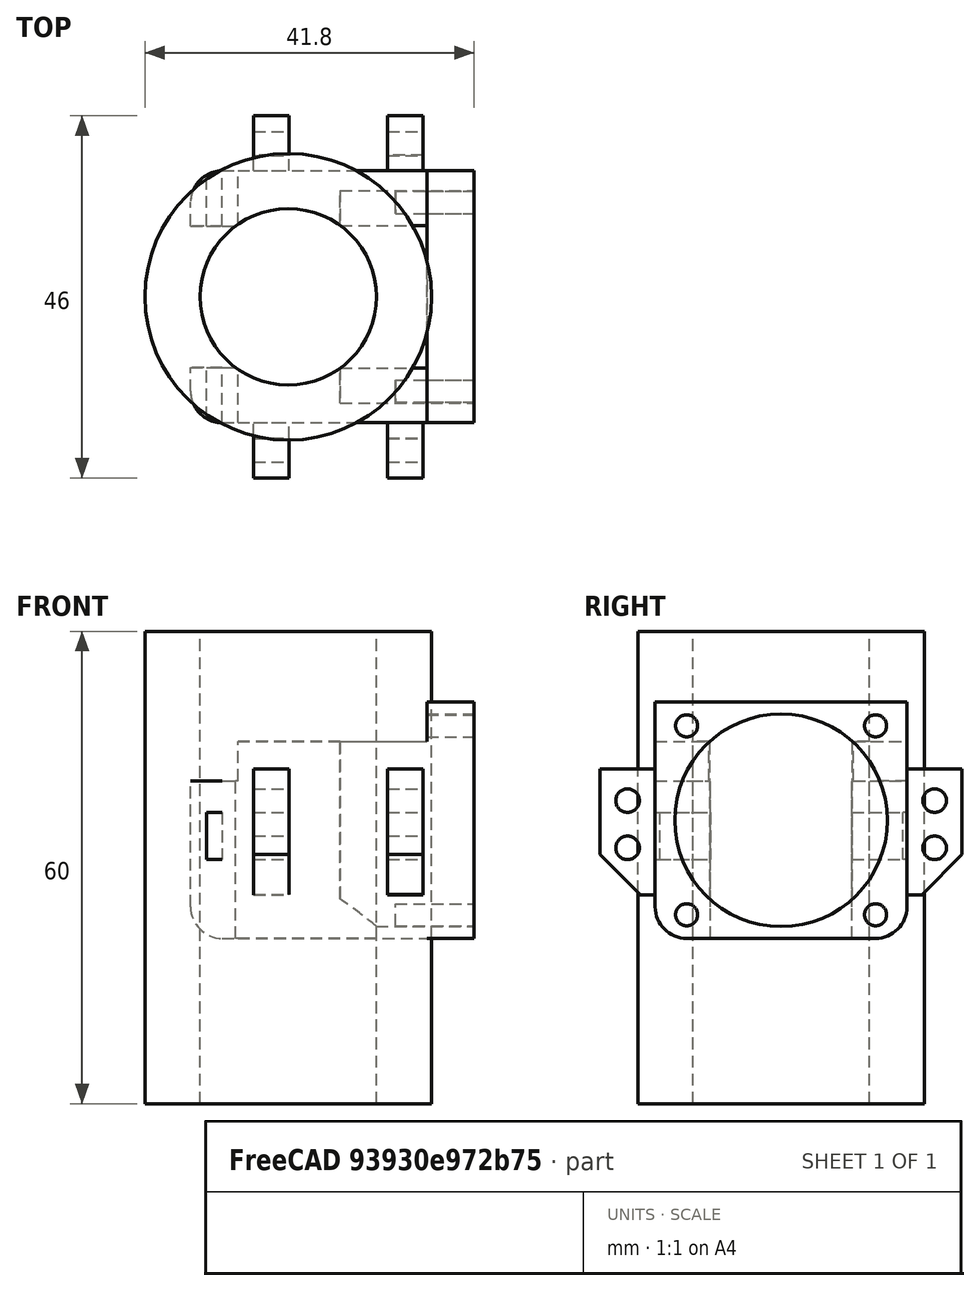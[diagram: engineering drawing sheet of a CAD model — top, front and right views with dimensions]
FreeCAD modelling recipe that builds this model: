
FCSTD DOCUMENT  (FreeCAD 0.15R4671 (Git))
Label: e3dv6
License: All rights reserved
LicenseURL: http://en.wikipedia.org/wiki/All_rights_reserved
objects: Part::Box×13, Part::Cylinder×12, Part::MultiFuse×6, Part::Fillet×4, Part::Cut×3, Mesh::Feature×2, Part::Feature×2
note: 40 computed .brp shape members not serialized (recipe doc carries the construction recipe); baked Part::Feature solids carry a one-line shape summary decoded from their .brp

FEATURE [Part::Box] Box  label="CubeMain"
  Height = 25
  Length = 24
  Width = 32
FEATURE [Part::Box] Box001  label="CubeFrontMask"
  Height = 30
  Length = 6
  Placement = pos=(24,0,0) rot=(0,0,1;0rad)
  Width = 32
FEATURE [Part::Cylinder] Cylinder  label="CylinderHeatSink"
  Angle = 360
  Height = 25
  Placement = pos=(6.4,16,0) rot=(0,0,1;0rad)
  Radius = 11.2
FEATURE [Part::Cylinder] Cylinder001  label="CylinderFan"
  Angle = 360
  Height = 18
  Placement = pos=(13,16,15) rot=(0,1,0;1.5708rad)
  Radius = 13.5
FEATURE [Part::Cylinder] Cylinder002  label="CylinderBL"
  Angle = 360
  Height = 20
  Placement = pos=(20,4,3) rot=(0,1,0;1.5708rad)
  Radius = 1.4
FEATURE [Part::Cylinder] Cylinder003  label="CylinderTL"
  Angle = 360
  Height = 20
  Placement = pos=(20,4,27) rot=(0,1,0;1.5708rad)
  Radius = 1.4
FEATURE [Part::Cylinder] Cylinder004  label="CylinderTB"
  Angle = 360
  Height = 20
  Placement = pos=(20,28,27) rot=(0,1,0;1.5708rad)
  Radius = 1.4
FEATURE [Part::Cylinder] Cylinder005  label="CylinderRB"
  Angle = 360
  Height = 20
  Placement = pos=(20,28,3) rot=(0,1,0;1.5708rad)
  Radius = 1.4
FEATURE [Part::MultiFuse] Fusion001  label="FusionFanScrews"
  Shapes = -> [Cylinder002,Cylinder003,Cylinder005,Cylinder004]
FEATURE [Part::Box] Box002  label="CubeZipTieL"
  Height = 20
  Length = 6
  Placement = pos=(-6,0,0) rot=(0,0,1;0rad)
  Width = 7
FEATURE [Part::Box] Box003  label="CubZipTieR"
  Height = 20
  Length = 6
  Placement = pos=(-6,25,0) rot=(0,0,1;0rad)
  Width = 7
FEATURE [Part::Box] Box004  label="CubeZipTieHor"
  Height = 6
  Length = 2
  Placement = pos=(-4,0,10) rot=(0,0,1;0rad)
  Width = 32
FEATURE [Part::Cylinder] Cylinder009
  Angle = 360
  Height = 40
  Placement = pos=(0,-3.5,12) rot=(0,1,0;1.5708rad)
  Radius = 1.5
FEATURE [Part::Cylinder] Cylinder010
  Angle = 360
  Height = 40
  Placement = pos=(0,-3.5,6) rot=(0,1,0;1.5708rad)
  Radius = 1.5
FEATURE [Part::Box] Box005  label="Cube005"
  Height = 16
  Length = 4.5
  Placement = pos=(2,-7,0) rot=(0,0,1;0rad)
  Width = 7
FEATURE [Part::Box] Box006  label="Cube006"
  Height = 16
  Length = 4.5
  Placement = pos=(19,-7,0) rot=(0,0,1;0rad)
  Width = 7
FEATURE [Part::Box] Box007  label="Cube007"
  Height = 16
  Length = 4.5
  Placement = pos=(2,32,0) rot=(0,0,1;0rad)
  Width = 7
FEATURE [Part::Box] Box008  label="Cube008"
  Height = 16
  Length = 4.5
  Placement = pos=(19,32,0) rot=(0,0,1;0rad)
  Width = 7
FEATURE [Part::Cylinder] Cylinder011
  Angle = 360
  Height = 40
  Placement = pos=(0,35.5,12) rot=(0,1,0;1.5708rad)
  Radius = 1.5
FEATURE [Part::Cylinder] Cylinder012
  Angle = 360
  Height = 40
  Placement = pos=(0,35.5,6) rot=(0,1,0;1.5708rad)
  Radius = 1.5
FEATURE [Part::MultiFuse] Fusion004  label="FusionWingScrews"
  Placement = pos=(0,0,5.5) rot=(0,0,1;0rad)
  Shapes = -> [Cylinder009,Cylinder010,Cylinder011,Cylinder012]
FEATURE [Part::Box] Box009  label="Cube009"
  Height = 10
  Length = 22
  Placement = pos=(2,-9,-7) rot=(1,0,0;0.785398rad)
  Width = 10
FEATURE [Part::Box] Box010  label="Cube010"
  Height = 10
  Length = 22
  Placement = pos=(2,41,-7) rot=(1,0,0;0.785398rad)
  Width = 10
FEATURE [Part::MultiFuse] Fusion006  label="FusionWings"
  Placement = pos=(0,0,5.5) rot=(0,0,1;0rad)
  Shapes = -> [Box005,Box006,Box007,Box008]
FEATURE [Part::MultiFuse] Fusion005  label="FusionWingCuts"
  Placement = pos=(0,0,5.5) rot=(0,0,1;0rad)
  Shapes = -> [Box009,Box010]
FEATURE [Part::MultiFuse] Fusion  label="FusionCUTS"
  Shapes = -> [Fusion001,Fusion005,Fusion004,Box004,Cylinder,Cylinder001]
FEATURE [Part::MultiFuse] Fusion007  label="FusionMain"
  Shapes = -> [Box,Box002,Fusion006,Box003,Box001]
FEATURE [Part::Fillet] Fillet
  Base = -> Fusion007
  Edges = 1 edges r=4: [Edge86]
FEATURE [Part::Fillet] Fillet001
  Base = -> Fillet
  Edges = 1 edges r=4: [Edge11]
FEATURE [Part::Fillet] Fillet002
  Base = -> Fillet001
  Edges = 1 edges r=4: [Edge66]
FEATURE [Part::Fillet] Fillet003
  Base = -> Fillet002
  Edges = 1 edges r=4: [Edge16]
FEATURE [Part::Cut] Cut  label="CutE3DV6Holder"
  Base = -> Fillet003
  Tool = -> Fusion
FEATURE [Mesh::Feature] E3D_v5_40mm_Duct
FEATURE [Part::Feature] E3D_v5_40mm_Duct001
  Placement = pos=(-37.5,50,14.2) rot=(0,0.965926,-0.258819;3.14159rad)
  shape: large baked B-rep (38 MB .brp); summary skipped
FEATURE [Part::Cylinder] Cylinder014  label="CylinderHeatSinkSignCenter"
  Angle = 360
  Height = 60
  Placement = pos=(6.4,16,-21) rot=(0,0,1;0rad)
  Radius = 11.2
FEATURE [Mesh::Feature] E3D_v5_40mm_Duct_Mirrored
  Placement = pos=(9.5,75,68) rot=(0.694747,-0.694747,-0.186157;3.50969rad)
FEATURE [Part::Feature] E3D_v5_40mm_Duct_Mirrored001
  shape: bbox 45.72 x 69.45 x 41.84 mm, 17238 faces, 0 solids (baked)
FEATURE [Part::Box] Box011  label="Cube"
  Height = 10
  Length = 100
  Placement = pos=(-43,7,-20) rot=(0,0,1;0rad)
  Width = 10
FEATURE [Part::Box] Box012  label="Cube011"
  Height = 10
  Length = 100
  Placement = pos=(-43,15,-20) rot=(0,0,1;0rad)
  Width = 10
FEATURE [Part::Cut] Cut001  label="CutRightFunDuct"
  Base = -> E3D_v5_40mm_Duct001
  Tool = -> Box011
FEATURE [Part::Cut] Cut002  label="CutLeftFunDuct"
  Base = -> E3D_v5_40mm_Duct_Mirrored001
  Tool = -> Box012
FEATURE [Part::Cylinder] Cylinder015  label="CylinderCenter"
  Angle = 360
  Height = 60
  Placement = pos=(6.4,16,-21) rot=(0,0,1;0rad)
  Radius = 18.2
